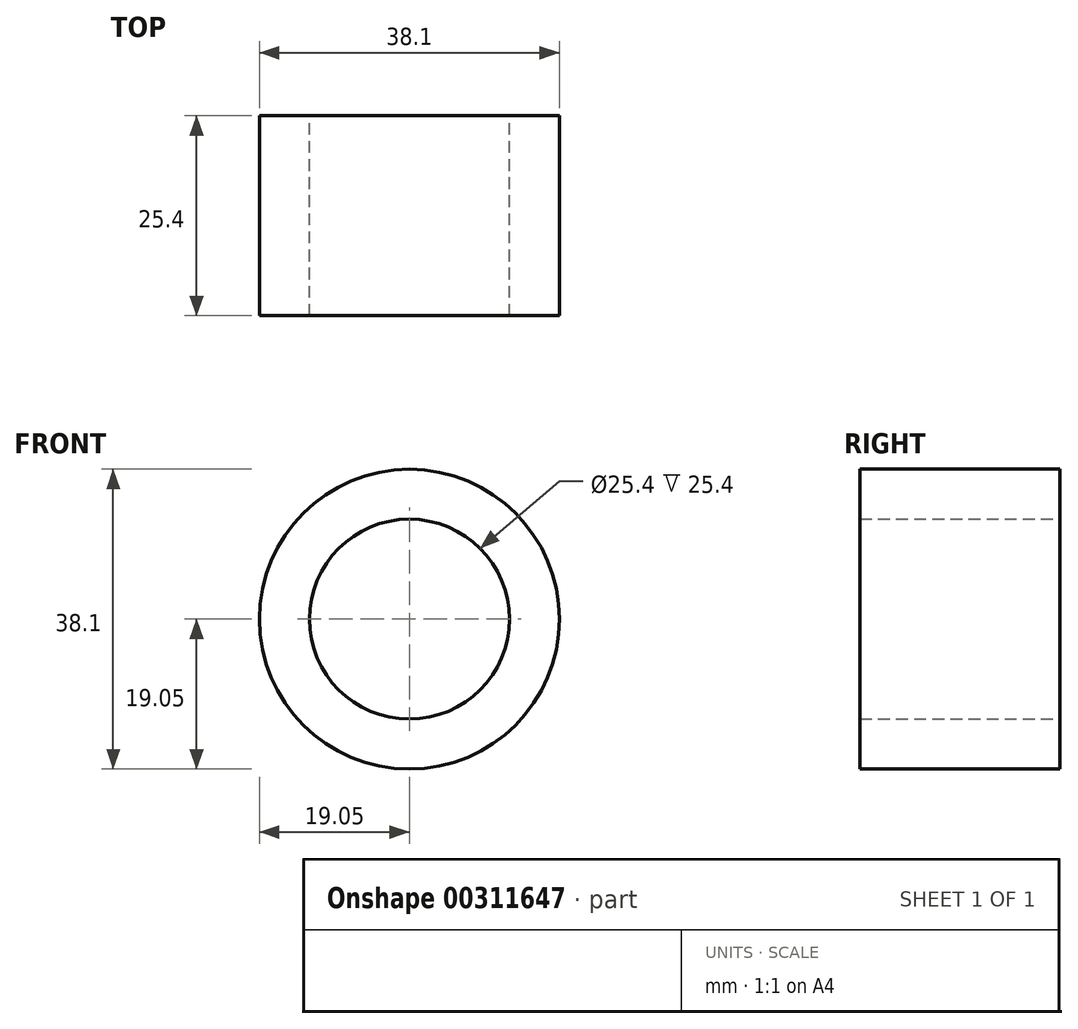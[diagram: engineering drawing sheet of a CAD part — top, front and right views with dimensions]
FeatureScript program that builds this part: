
annotation { "Feature Type Name" : "Feature", "Feature Type Description" : "" }
export const myFeature = defineFeature(function(context is Context, id is Id, definition is map)
    precondition{}
    {
        {
            var Q0;
            Q0=qCreatedBy(makeId("Front.planeOp"),FACE);
            var sketch = newSketch(context, id + "F0", { "sketchPlane" : qUnion([Q0])});
            skCircle(sketch, "E0", {"center": v(0, 0) * mm, "radius": 12.7 * mm});
            skCircle(sketch, "E1", {"center": v(0, 0) * mm, "radius": 19.05 * mm});
            skSolve(sketch);
        }
        {
            var Q0;
            Q0 = qSketchRegion(id + "F0", true);
            extrude(context, id + "F1", {"entities" : qUnion([Q0]), "depth" : 25.4 * mm});
        }
    });
